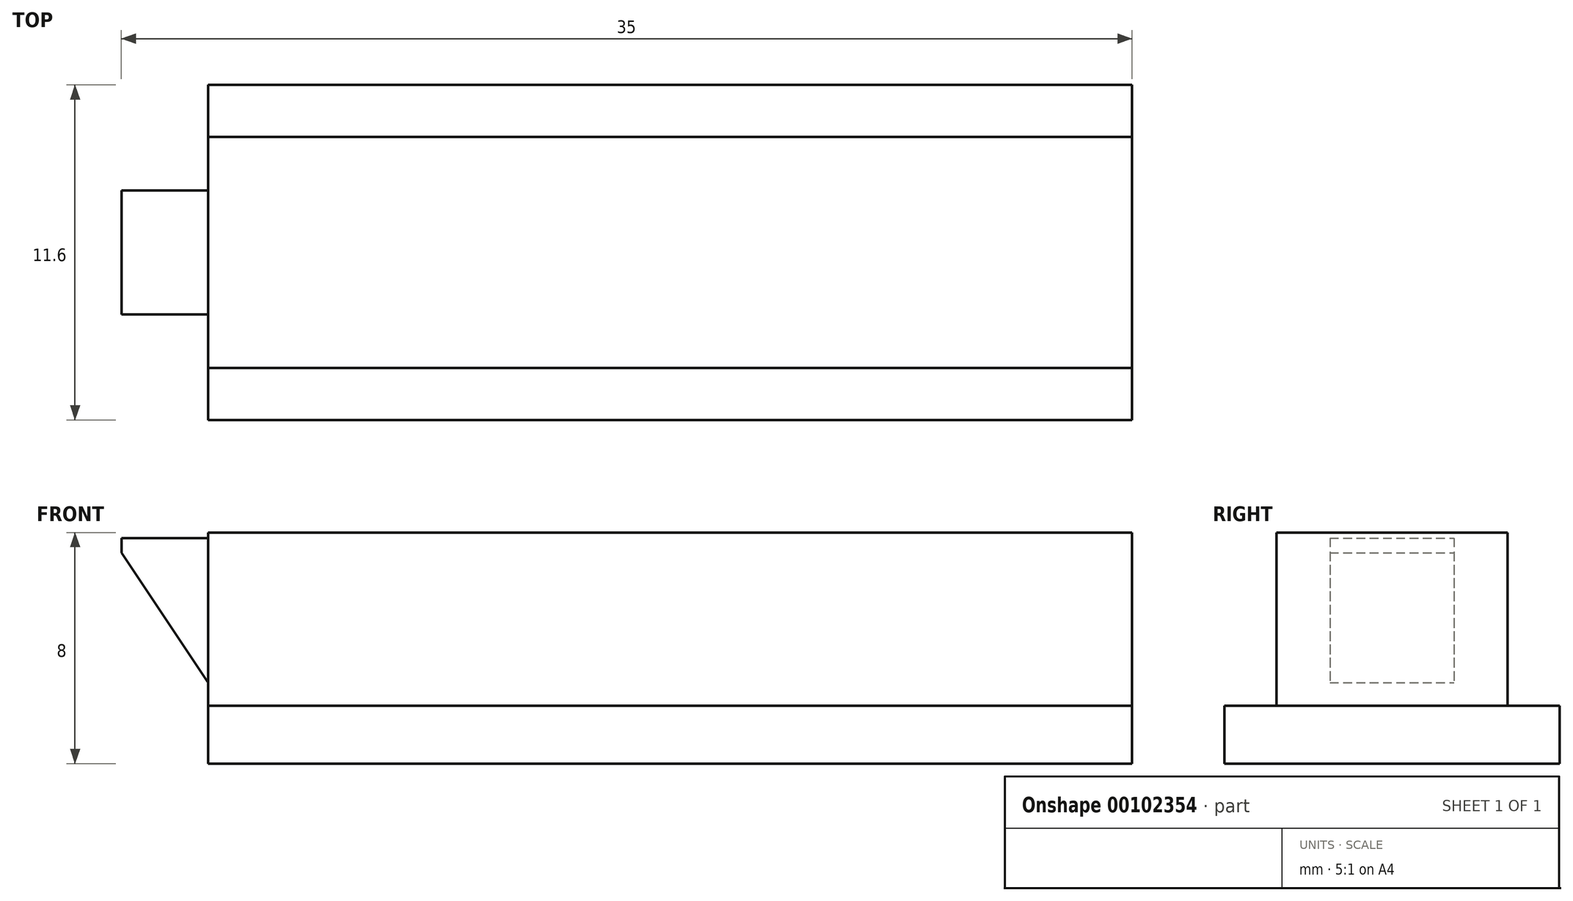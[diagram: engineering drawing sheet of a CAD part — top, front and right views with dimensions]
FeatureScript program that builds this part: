
annotation { "Feature Type Name" : "Feature", "Feature Type Description" : "" }
export const myFeature = defineFeature(function(context is Context, id is Id, definition is map)
    precondition{}
    {
        {
            var Q0;
            Q0=qCreatedBy(makeId("Front.planeOp"),FACE);
            var sketch = newSketch(context, id + "F0", { "sketchPlane" : qUnion([Q0])});
            skLineSegment(sketch, "E0", {"start": v(-13.84, 0) * mm, "end": v(18.16, 0) * mm});
            skLineSegment(sketch, "E1", {"start": v(18.16, 0) * mm, "end": v(18.16, 8) * mm});
            skLineSegment(sketch, "E2", {"start": v(18.16, 8) * mm, "end": v(-13.84, 8) * mm});
            skLineSegment(sketch, "E3", {"start": v(-13.84, 8) * mm, "end": v(-13.84, 0) * mm});
            skLineSegment(sketch, "E4", {"start": v(-13.84, 7.8) * mm, "end": v(-16.84, 7.8) * mm});
            skLineSegment(sketch, "E5", {"start": v(-16.84, 7.8) * mm, "end": v(-16.84, 7.3) * mm});
            skLineSegment(sketch, "E6", {"start": v(-16.84, 7.3) * mm, "end": v(-13.84, 2.8) * mm});
            skLineSegment(sketch, "E7.0", {"start": v(-13.84, 2) * mm, "end": v(18.16, 2) * mm});
            skSolve(sketch);
        }
        {
            var Q0;
            {var subQ3=sQuery(id+"F0.wireOp",EDGE,"E2");Q0=makeQuery(id+"F0.imprint","IMPRINT",FACE,{"disambiguationData":[TD([[makeQuery(id+"F0.imprint","IMPRINT",EDGE,{"derivedFrom":subQ3}),1.0]])]});}
            extrude(context, id + "F1", {"entities" : qUnion([Q0]), "endBound" : BoundingType.SYMMETRIC, "depth" : 8 * mm});
        }
        {
            var Q0;
            {var subQ0=sQuery(id+"F0.wireOp",EDGE,"E4");Q0=makeQuery(id+"F0.imprint","IMPRINT",FACE,{"disambiguationData":[TD([[makeQuery(id+"F0.imprint","IMPRINT",EDGE,{"derivedFrom":subQ0}),1.0]])]});}
            extrude(context, id + "F2", {"entities" : qUnion([Q0]), "endBound" : BoundingType.SYMMETRIC, "depth" : 4.3 * mm});
        }
        {
            var Q0;
            {var subQ0=sQuery(id+"F0.wireOp",EDGE,"E0");Q0=makeQuery(id+"F0.imprint","IMPRINT",FACE,{"disambiguationData":[TD([[makeQuery(id+"F0.imprint","IMPRINT",EDGE,{"derivedFrom":subQ0}),1.0]])]});}
            extrude(context, id + "F3", {"entities" : qUnion([Q0]), "endBound" : BoundingType.SYMMETRIC, "depth" : 11.6 * mm});
        }
    });
